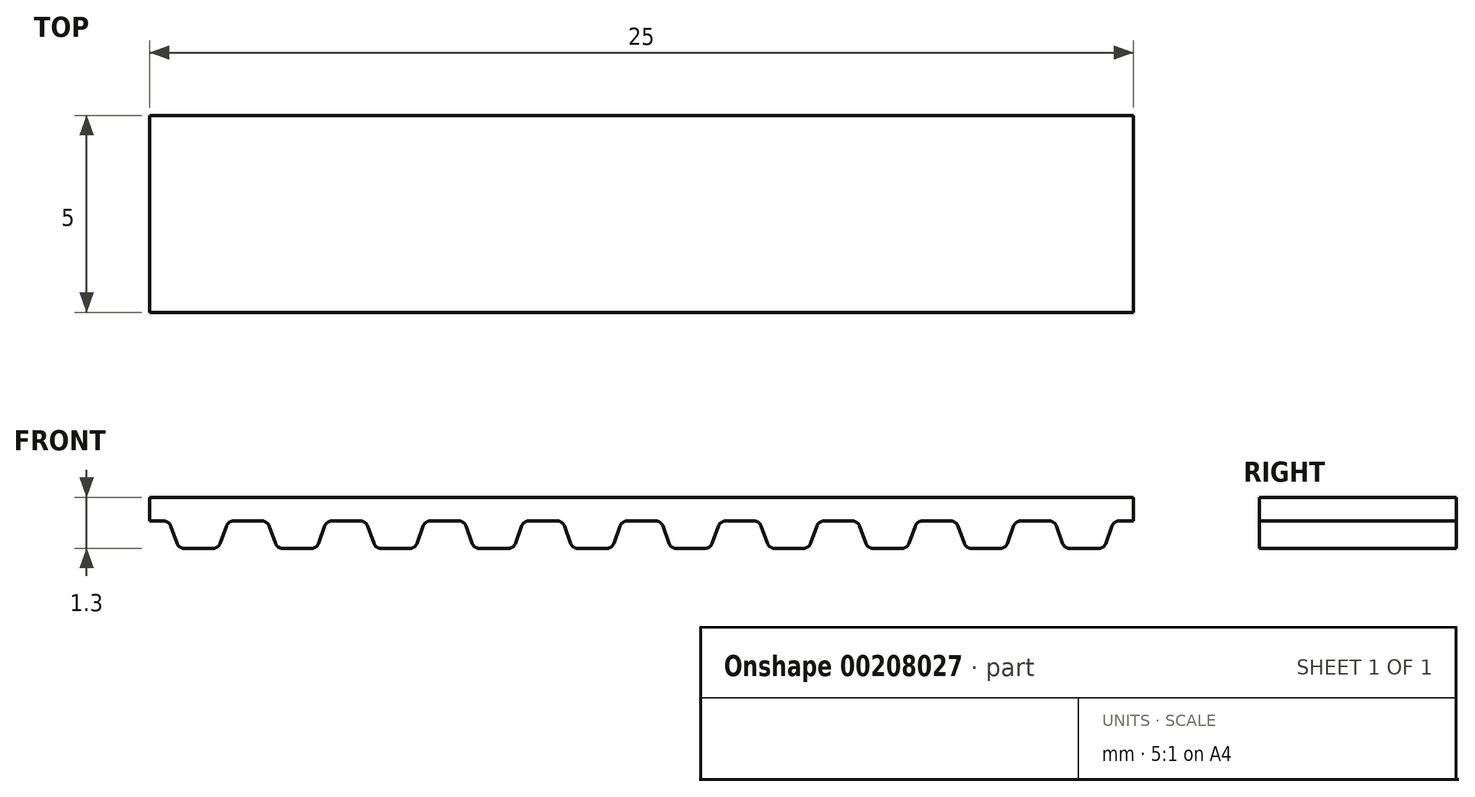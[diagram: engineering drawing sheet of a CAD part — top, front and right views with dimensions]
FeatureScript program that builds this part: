
annotation { "Feature Type Name" : "Feature", "Feature Type Description" : "" }
export const myFeature = defineFeature(function(context is Context, id is Id, definition is map)
    precondition{}
    {
        {
            var Q0;
            Q0=qCreatedBy(makeId("Front.planeOp"),FACE);
            var sketch = newSketch(context, id + "F0", { "sketchPlane" : qUnion([Q0])});
            skLineSegment(sketch, "E0.bottom", {"start": v(-21.07, 19.92) * mm, "end": v(-19.82, 19.92) * mm});
            skLineSegment(sketch, "E0.top", {"start": v(-20.18, 19.32) * mm, "end": v(-19.82, 19.32) * mm});
            skLineSegment(sketch, "E1", {"start": v(-21.07, 18.62) * mm, "end": v(-20.71, 18.62) * mm});
            skLineSegment(sketch, "E2", {"start": v(-20.52, 18.75) * mm, "end": v(-20.37, 19.19) * mm});
            skPoint(sketch, "E3.visualSharp", {"position": v(-20.57, 18.62) * mm});
            skArc(sketch, "E3.filletArc", {"start": v(-20.71, 18.62) * mm, "mid": v(-20.6, 18.65) * mm, "end": v(-20.52, 18.75) * mm});
            skArc(sketch, "E4.filletArc", {"start": v(-20.18, 19.32) * mm, "mid": v(-20.3, 19.28) * mm, "end": v(-20.37, 19.19) * mm});
            skLineSegment(sketch, "E5.MirrorCS", {"start": v(-21.07, 19.92) * mm, "end": v(-22.32, 19.92) * mm});
            skLineSegment(sketch, "E6.MirrorCS", {"start": v(-22.32, 19.92) * mm, "end": v(-22.32, 19.32) * mm});
            skLineSegment(sketch, "E7.MirrorCS", {"start": v(-21.97, 19.32) * mm, "end": v(-22.32, 19.32) * mm});
            skArc(sketch, "E8.MirrorCS", {"start": v(-21.97, 19.32) * mm, "mid": v(-21.85, 19.28) * mm, "end": v(-21.78, 19.19) * mm});
            skLineSegment(sketch, "E9.MirrorCS", {"start": v(-21.62, 18.75) * mm, "end": v(-21.78, 19.19) * mm});
            skArc(sketch, "E10.MirrorCS", {"start": v(-21.43, 18.62) * mm, "mid": v(-21.55, 18.65) * mm, "end": v(-21.62, 18.75) * mm});
            skLineSegment(sketch, "E11.MirrorCS", {"start": v(-21.07, 18.62) * mm, "end": v(-21.43, 18.62) * mm});
            skLineSegment(sketch, "E12.1.0.0", {"start": v(-18.57, 19.92) * mm, "end": v(-17.32, 19.92) * mm});
            skLineSegment(sketch, "E12.1.0.1", {"start": v(-18.57, 19.92) * mm, "end": v(-19.82, 19.92) * mm});
            skLineSegment(sketch, "E12.1.0.3", {"start": v(-19.47, 19.32) * mm, "end": v(-19.82, 19.32) * mm});
            skArc(sketch, "E12.1.0.4", {"start": v(-19.47, 19.32) * mm, "mid": v(-19.35, 19.28) * mm, "end": v(-19.28, 19.19) * mm});
            skLineSegment(sketch, "E12.1.0.5", {"start": v(-19.12, 18.75) * mm, "end": v(-19.28, 19.19) * mm});
            skArc(sketch, "E12.1.0.6", {"start": v(-18.93, 18.62) * mm, "mid": v(-19.05, 18.65) * mm, "end": v(-19.12, 18.75) * mm});
            skLineSegment(sketch, "E12.1.0.7", {"start": v(-18.57, 18.62) * mm, "end": v(-18.93, 18.62) * mm});
            skLineSegment(sketch, "E12.1.0.8", {"start": v(-18.57, 18.62) * mm, "end": v(-18.21, 18.62) * mm});
            skArc(sketch, "E12.1.0.9", {"start": v(-18.21, 18.62) * mm, "mid": v(-18.1, 18.65) * mm, "end": v(-18.02, 18.75) * mm});
            skLineSegment(sketch, "E12.1.0.10", {"start": v(-18.02, 18.75) * mm, "end": v(-17.87, 19.19) * mm});
            skArc(sketch, "E12.1.0.11", {"start": v(-17.68, 19.32) * mm, "mid": v(-17.8, 19.28) * mm, "end": v(-17.87, 19.19) * mm});
            skLineSegment(sketch, "E12.1.0.12", {"start": v(-17.68, 19.32) * mm, "end": v(-17.32, 19.32) * mm});
            skLineSegment(sketch, "E12.2.0.0", {"start": v(-16.07, 19.92) * mm, "end": v(-14.82, 19.92) * mm});
            skLineSegment(sketch, "E12.2.0.1", {"start": v(-16.07, 19.92) * mm, "end": v(-17.32, 19.92) * mm});
            skLineSegment(sketch, "E12.2.0.3", {"start": v(-16.97, 19.32) * mm, "end": v(-17.32, 19.32) * mm});
            skArc(sketch, "E12.2.0.4", {"start": v(-16.97, 19.32) * mm, "mid": v(-16.85, 19.28) * mm, "end": v(-16.78, 19.19) * mm});
            skLineSegment(sketch, "E12.2.0.5", {"start": v(-16.62, 18.75) * mm, "end": v(-16.78, 19.19) * mm});
            skArc(sketch, "E12.2.0.6", {"start": v(-16.43, 18.62) * mm, "mid": v(-16.55, 18.65) * mm, "end": v(-16.62, 18.75) * mm});
            skLineSegment(sketch, "E12.2.0.7", {"start": v(-16.07, 18.62) * mm, "end": v(-16.43, 18.62) * mm});
            skLineSegment(sketch, "E12.2.0.8", {"start": v(-16.07, 18.62) * mm, "end": v(-15.71, 18.62) * mm});
            skArc(sketch, "E12.2.0.9", {"start": v(-15.71, 18.62) * mm, "mid": v(-15.6, 18.65) * mm, "end": v(-15.52, 18.75) * mm});
            skLineSegment(sketch, "E12.2.0.10", {"start": v(-15.52, 18.75) * mm, "end": v(-15.37, 19.19) * mm});
            skArc(sketch, "E12.2.0.11", {"start": v(-15.18, 19.32) * mm, "mid": v(-15.3, 19.28) * mm, "end": v(-15.37, 19.19) * mm});
            skLineSegment(sketch, "E12.2.0.12", {"start": v(-15.18, 19.32) * mm, "end": v(-14.82, 19.32) * mm});
            skLineSegment(sketch, "E12.3.0.0", {"start": v(-13.57, 19.92) * mm, "end": v(-12.32, 19.92) * mm});
            skLineSegment(sketch, "E12.3.0.1", {"start": v(-13.57, 19.92) * mm, "end": v(-14.82, 19.92) * mm});
            skLineSegment(sketch, "E12.3.0.3", {"start": v(-14.47, 19.32) * mm, "end": v(-14.82, 19.32) * mm});
            skArc(sketch, "E12.3.0.4", {"start": v(-14.47, 19.32) * mm, "mid": v(-14.35, 19.28) * mm, "end": v(-14.28, 19.19) * mm});
            skLineSegment(sketch, "E12.3.0.5", {"start": v(-14.12, 18.75) * mm, "end": v(-14.28, 19.19) * mm});
            skArc(sketch, "E12.3.0.6", {"start": v(-13.93, 18.62) * mm, "mid": v(-14.05, 18.65) * mm, "end": v(-14.12, 18.75) * mm});
            skLineSegment(sketch, "E12.3.0.7", {"start": v(-13.57, 18.62) * mm, "end": v(-13.93, 18.62) * mm});
            skLineSegment(sketch, "E12.3.0.8", {"start": v(-13.57, 18.62) * mm, "end": v(-13.21, 18.62) * mm});
            skArc(sketch, "E12.3.0.9", {"start": v(-13.21, 18.62) * mm, "mid": v(-13.1, 18.65) * mm, "end": v(-13.02, 18.75) * mm});
            skLineSegment(sketch, "E12.3.0.10", {"start": v(-13.02, 18.75) * mm, "end": v(-12.87, 19.19) * mm});
            skArc(sketch, "E12.3.0.11", {"start": v(-12.68, 19.32) * mm, "mid": v(-12.8, 19.28) * mm, "end": v(-12.87, 19.19) * mm});
            skLineSegment(sketch, "E12.3.0.12", {"start": v(-12.68, 19.32) * mm, "end": v(-12.32, 19.32) * mm});
            skLineSegment(sketch, "E12.4.0.0", {"start": v(-11.07, 19.92) * mm, "end": v(-9.82, 19.92) * mm});
            skLineSegment(sketch, "E12.4.0.1", {"start": v(-11.07, 19.92) * mm, "end": v(-12.32, 19.92) * mm});
            skLineSegment(sketch, "E12.4.0.3", {"start": v(-11.97, 19.32) * mm, "end": v(-12.32, 19.32) * mm});
            skArc(sketch, "E12.4.0.4", {"start": v(-11.97, 19.32) * mm, "mid": v(-11.85, 19.28) * mm, "end": v(-11.78, 19.19) * mm});
            skLineSegment(sketch, "E12.4.0.5", {"start": v(-11.62, 18.75) * mm, "end": v(-11.78, 19.19) * mm});
            skArc(sketch, "E12.4.0.6", {"start": v(-11.43, 18.62) * mm, "mid": v(-11.55, 18.65) * mm, "end": v(-11.62, 18.75) * mm});
            skLineSegment(sketch, "E12.4.0.7", {"start": v(-11.07, 18.62) * mm, "end": v(-11.43, 18.62) * mm});
            skLineSegment(sketch, "E12.4.0.8", {"start": v(-11.07, 18.62) * mm, "end": v(-10.71, 18.62) * mm});
            skArc(sketch, "E12.4.0.9", {"start": v(-10.71, 18.62) * mm, "mid": v(-10.6, 18.65) * mm, "end": v(-10.52, 18.75) * mm});
            skLineSegment(sketch, "E12.4.0.10", {"start": v(-10.52, 18.75) * mm, "end": v(-10.37, 19.19) * mm});
            skArc(sketch, "E12.4.0.11", {"start": v(-10.18, 19.32) * mm, "mid": v(-10.3, 19.28) * mm, "end": v(-10.37, 19.19) * mm});
            skLineSegment(sketch, "E12.4.0.12", {"start": v(-10.18, 19.32) * mm, "end": v(-9.82, 19.32) * mm});
            skLineSegment(sketch, "E12.5.0.0", {"start": v(-8.57, 19.92) * mm, "end": v(-7.32, 19.92) * mm});
            skLineSegment(sketch, "E12.5.0.1", {"start": v(-8.57, 19.92) * mm, "end": v(-9.82, 19.92) * mm});
            skLineSegment(sketch, "E12.5.0.3", {"start": v(-9.47, 19.32) * mm, "end": v(-9.82, 19.32) * mm});
            skArc(sketch, "E12.5.0.4", {"start": v(-9.47, 19.32) * mm, "mid": v(-9.35, 19.28) * mm, "end": v(-9.28, 19.19) * mm});
            skLineSegment(sketch, "E12.5.0.5", {"start": v(-9.12, 18.75) * mm, "end": v(-9.28, 19.19) * mm});
            skArc(sketch, "E12.5.0.6", {"start": v(-8.93, 18.62) * mm, "mid": v(-9.05, 18.65) * mm, "end": v(-9.12, 18.75) * mm});
            skLineSegment(sketch, "E12.5.0.7", {"start": v(-8.57, 18.62) * mm, "end": v(-8.93, 18.62) * mm});
            skLineSegment(sketch, "E12.5.0.8", {"start": v(-8.57, 18.62) * mm, "end": v(-8.21, 18.62) * mm});
            skArc(sketch, "E12.5.0.9", {"start": v(-8.21, 18.62) * mm, "mid": v(-8.1, 18.65) * mm, "end": v(-8.02, 18.75) * mm});
            skLineSegment(sketch, "E12.5.0.10", {"start": v(-8.02, 18.75) * mm, "end": v(-7.87, 19.19) * mm});
            skArc(sketch, "E12.5.0.11", {"start": v(-7.68, 19.32) * mm, "mid": v(-7.8, 19.28) * mm, "end": v(-7.87, 19.19) * mm});
            skLineSegment(sketch, "E12.5.0.12", {"start": v(-7.68, 19.32) * mm, "end": v(-7.32, 19.32) * mm});
            skLineSegment(sketch, "E12.6.0.0", {"start": v(-6.07, 19.92) * mm, "end": v(-4.82, 19.92) * mm});
            skLineSegment(sketch, "E12.6.0.1", {"start": v(-6.07, 19.92) * mm, "end": v(-7.32, 19.92) * mm});
            skLineSegment(sketch, "E12.6.0.3", {"start": v(-6.97, 19.32) * mm, "end": v(-7.32, 19.32) * mm});
            skArc(sketch, "E12.6.0.4", {"start": v(-6.97, 19.32) * mm, "mid": v(-6.85, 19.28) * mm, "end": v(-6.78, 19.19) * mm});
            skLineSegment(sketch, "E12.6.0.5", {"start": v(-6.62, 18.75) * mm, "end": v(-6.78, 19.19) * mm});
            skArc(sketch, "E12.6.0.6", {"start": v(-6.43, 18.62) * mm, "mid": v(-6.55, 18.65) * mm, "end": v(-6.62, 18.75) * mm});
            skLineSegment(sketch, "E12.6.0.7", {"start": v(-6.07, 18.62) * mm, "end": v(-6.43, 18.62) * mm});
            skLineSegment(sketch, "E12.6.0.8", {"start": v(-6.07, 18.62) * mm, "end": v(-5.71, 18.62) * mm});
            skArc(sketch, "E12.6.0.9", {"start": v(-5.71, 18.62) * mm, "mid": v(-5.6, 18.65) * mm, "end": v(-5.52, 18.75) * mm});
            skLineSegment(sketch, "E12.6.0.10", {"start": v(-5.52, 18.75) * mm, "end": v(-5.37, 19.19) * mm});
            skArc(sketch, "E12.6.0.11", {"start": v(-5.18, 19.32) * mm, "mid": v(-5.3, 19.28) * mm, "end": v(-5.37, 19.19) * mm});
            skLineSegment(sketch, "E12.6.0.12", {"start": v(-5.18, 19.32) * mm, "end": v(-4.82, 19.32) * mm});
            skLineSegment(sketch, "E12.7.0.0", {"start": v(-3.57, 19.92) * mm, "end": v(-2.32, 19.92) * mm});
            skLineSegment(sketch, "E12.7.0.1", {"start": v(-3.57, 19.92) * mm, "end": v(-4.82, 19.92) * mm});
            skLineSegment(sketch, "E12.7.0.3", {"start": v(-4.47, 19.32) * mm, "end": v(-4.82, 19.32) * mm});
            skArc(sketch, "E12.7.0.4", {"start": v(-4.47, 19.32) * mm, "mid": v(-4.35, 19.28) * mm, "end": v(-4.28, 19.19) * mm});
            skLineSegment(sketch, "E12.7.0.5", {"start": v(-4.12, 18.75) * mm, "end": v(-4.28, 19.19) * mm});
            skArc(sketch, "E12.7.0.6", {"start": v(-3.93, 18.62) * mm, "mid": v(-4.05, 18.65) * mm, "end": v(-4.12, 18.75) * mm});
            skLineSegment(sketch, "E12.7.0.7", {"start": v(-3.57, 18.62) * mm, "end": v(-3.93, 18.62) * mm});
            skLineSegment(sketch, "E12.7.0.8", {"start": v(-3.57, 18.62) * mm, "end": v(-3.21, 18.62) * mm});
            skArc(sketch, "E12.7.0.9", {"start": v(-3.21, 18.62) * mm, "mid": v(-3.1, 18.65) * mm, "end": v(-3.02, 18.75) * mm});
            skLineSegment(sketch, "E12.7.0.10", {"start": v(-3.02, 18.75) * mm, "end": v(-2.87, 19.19) * mm});
            skArc(sketch, "E12.7.0.11", {"start": v(-2.68, 19.32) * mm, "mid": v(-2.8, 19.28) * mm, "end": v(-2.87, 19.19) * mm});
            skLineSegment(sketch, "E12.7.0.12", {"start": v(-2.68, 19.32) * mm, "end": v(-2.32, 19.32) * mm});
            skLineSegment(sketch, "E12.8.0.0", {"start": v(-1.07, 19.92) * mm, "end": v(0.18, 19.92) * mm});
            skLineSegment(sketch, "E12.8.0.1", {"start": v(-1.07, 19.92) * mm, "end": v(-2.32, 19.92) * mm});
            skLineSegment(sketch, "E12.8.0.3", {"start": v(-1.97, 19.32) * mm, "end": v(-2.32, 19.32) * mm});
            skArc(sketch, "E12.8.0.4", {"start": v(-1.97, 19.32) * mm, "mid": v(-1.85, 19.28) * mm, "end": v(-1.78, 19.19) * mm});
            skLineSegment(sketch, "E12.8.0.5", {"start": v(-1.62, 18.75) * mm, "end": v(-1.78, 19.19) * mm});
            skArc(sketch, "E12.8.0.6", {"start": v(-1.43, 18.62) * mm, "mid": v(-1.55, 18.65) * mm, "end": v(-1.62, 18.75) * mm});
            skLineSegment(sketch, "E12.8.0.7", {"start": v(-1.07, 18.62) * mm, "end": v(-1.43, 18.62) * mm});
            skLineSegment(sketch, "E12.8.0.8", {"start": v(-1.07, 18.62) * mm, "end": v(-0.71, 18.62) * mm});
            skArc(sketch, "E12.8.0.9", {"start": v(-0.71, 18.62) * mm, "mid": v(-0.6, 18.65) * mm, "end": v(-0.52, 18.75) * mm});
            skLineSegment(sketch, "E12.8.0.10", {"start": v(-0.52, 18.75) * mm, "end": v(-0.37, 19.19) * mm});
            skArc(sketch, "E12.8.0.11", {"start": v(-0.18, 19.32) * mm, "mid": v(-0.3, 19.28) * mm, "end": v(-0.37, 19.19) * mm});
            skLineSegment(sketch, "E12.8.0.12", {"start": v(-0.18, 19.32) * mm, "end": v(0.18, 19.32) * mm});
            skLineSegment(sketch, "E12.9.0.0", {"start": v(1.43, 19.92) * mm, "end": v(2.68, 19.92) * mm});
            skLineSegment(sketch, "E12.9.0.1", {"start": v(1.43, 19.92) * mm, "end": v(0.18, 19.92) * mm});
            skLineSegment(sketch, "E12.9.0.3", {"start": v(0.53, 19.32) * mm, "end": v(0.18, 19.32) * mm});
            skArc(sketch, "E12.9.0.4", {"start": v(0.53, 19.32) * mm, "mid": v(0.65, 19.28) * mm, "end": v(0.72, 19.19) * mm});
            skLineSegment(sketch, "E12.9.0.5", {"start": v(0.88, 18.75) * mm, "end": v(0.72, 19.19) * mm});
            skArc(sketch, "E12.9.0.6", {"start": v(1.07, 18.62) * mm, "mid": v(0.95, 18.65) * mm, "end": v(0.88, 18.75) * mm});
            skLineSegment(sketch, "E12.9.0.7", {"start": v(1.43, 18.62) * mm, "end": v(1.07, 18.62) * mm});
            skLineSegment(sketch, "E12.9.0.8", {"start": v(1.43, 18.62) * mm, "end": v(1.79, 18.62) * mm});
            skArc(sketch, "E12.9.0.9", {"start": v(1.79, 18.62) * mm, "mid": v(1.9, 18.65) * mm, "end": v(1.98, 18.75) * mm});
            skLineSegment(sketch, "E12.9.0.10", {"start": v(1.98, 18.75) * mm, "end": v(2.13, 19.19) * mm});
            skArc(sketch, "E12.9.0.11", {"start": v(2.32, 19.32) * mm, "mid": v(2.2, 19.28) * mm, "end": v(2.13, 19.19) * mm});
            skLineSegment(sketch, "E12.9.0.12", {"start": v(2.32, 19.32) * mm, "end": v(2.68, 19.32) * mm});
            skLineSegment(sketch, "E12.9.0.13", {"start": v(2.68, 19.92) * mm, "end": v(2.68, 19.32) * mm});
            skLineSegment(sketch, "E12.direction1", {"start": v(-21.07, 19.92) * mm, "end": v(-18.57, 19.92) * mm, "construction": true});
            skSolve(sketch);
        }
        {
            var Q0;
            Q0=makeQuery(id+"F0.imprint","IMPRINT",FACE,{"disambiguationData":[TD([[makeQuery(id+"F0.imprint","IMPRINT",EDGE,{"derivedFrom":sQuery(id+"F0.wireOp",EDGE,"E0.bottom")}),-1.0]])]});
            extrude(context, id + "F1", {"entities" : qUnion([Q0]), "depth" : 5 * mm});
        }
    });
